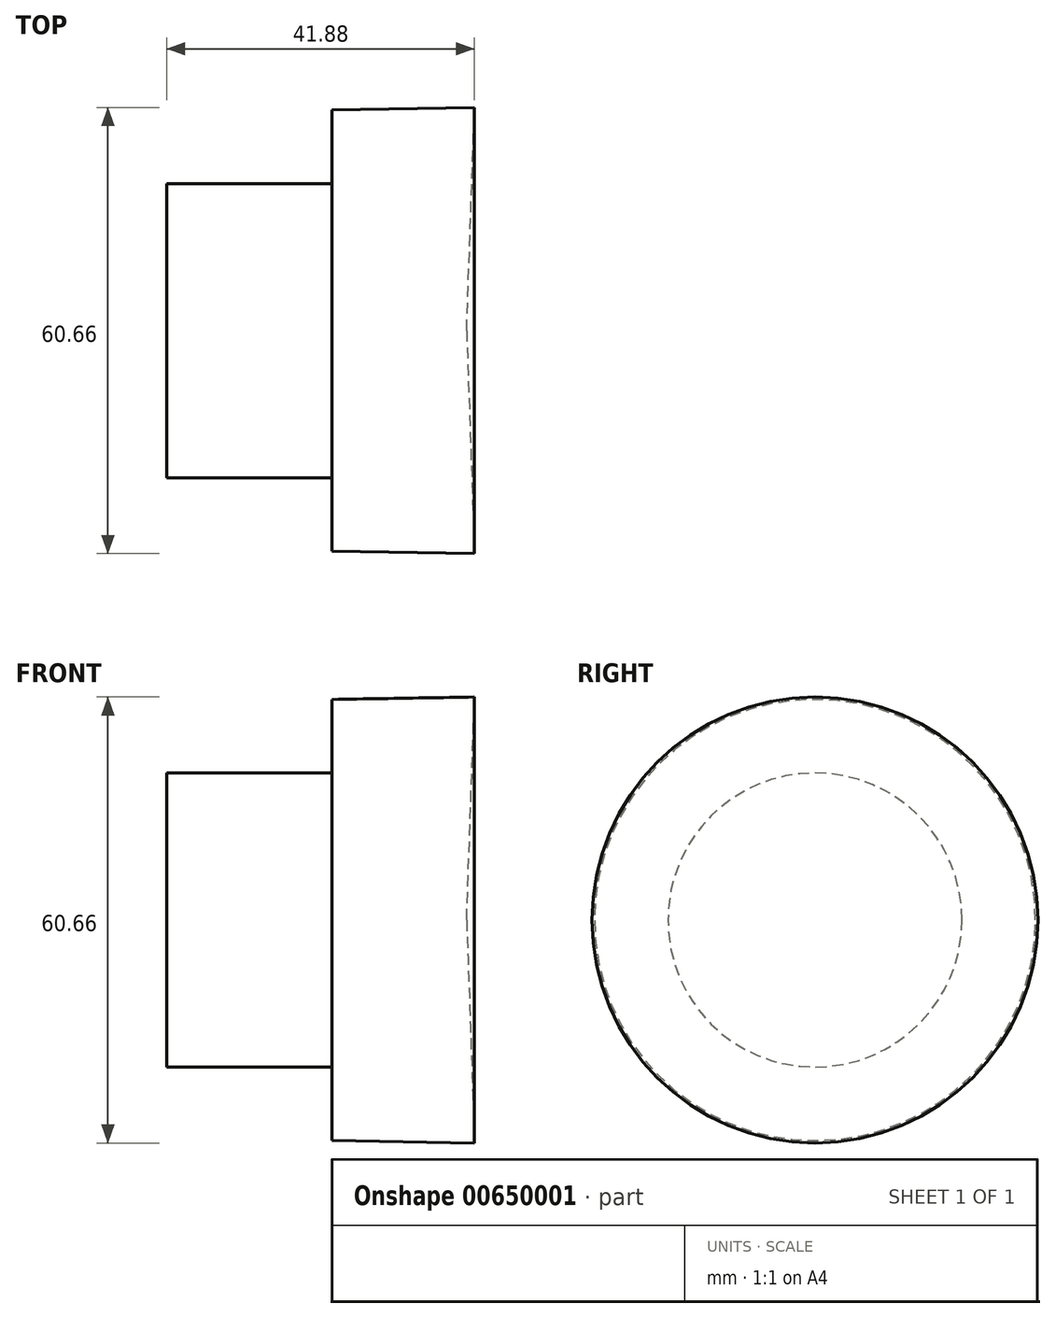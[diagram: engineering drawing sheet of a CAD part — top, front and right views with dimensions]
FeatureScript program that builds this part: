
annotation { "Feature Type Name" : "Feature", "Feature Type Description" : "" }
export const myFeature = defineFeature(function(context is Context, id is Id, definition is map)
    precondition{}
    {
        {
            var Q0;
            Q0=qCreatedBy(makeId("Front.planeOp"),FACE);
            var sketch = newSketch(context, id + "F0", { "sketchPlane" : qUnion([Q0])});
            skLineSegment(sketch, "E0", {"start": v(0, 0) * mm, "end": v(51.07, 0) * mm, "construction": true});
            skSolve(sketch);
        }
        {
            var Q0;
            Q0=qCreatedBy(makeId("Front.planeOp"),FACE);
            var sketch = newSketch(context, id + "F1", { "sketchPlane" : qUnion([Q0])});
            skLineSegment(sketch, "E1", {"start": v(0, 0) * mm, "end": v(0, 20) * mm});
            skLineSegment(sketch, "E2", {"start": v(0, 20) * mm, "end": v(22.52, 20) * mm});
            skLineSegment(sketch, "E3", {"start": v(22.52, 20) * mm, "end": v(22.52, 30) * mm});
            skLineSegment(sketch, "E4", {"start": v(22.52, 30) * mm, "end": v(41.88, 30.33) * mm});
            skLineSegment(sketch, "E5", {"start": v(41.88, 30.33) * mm, "end": v(40.82, 0) * mm});
            skLineSegment(sketch, "E6", {"start": v(40.82, 0) * mm, "end": v(0, 0) * mm});
            skSolve(sketch);
        }
        {
            var Q0;
            Q0=makeQuery(id+"F1.imprint","IMPRINT",FACE,{"disambiguationData":[TD([[makeQuery(id+"F1.imprint","IMPRINT",EDGE,{"derivedFrom":sQuery(id+"F1.wireOp",EDGE,"E1")}),-1.0]])]});
            var Q1;
            Q1=sQuery(id+"F0.wireOp",EDGE,"E0");
            revolve(context, id + "F2", {"entities" : qUnion([Q0]), "axis" : qUnion([Q1]), "revolveType" : RevolveType.FULL});
        }
    });
